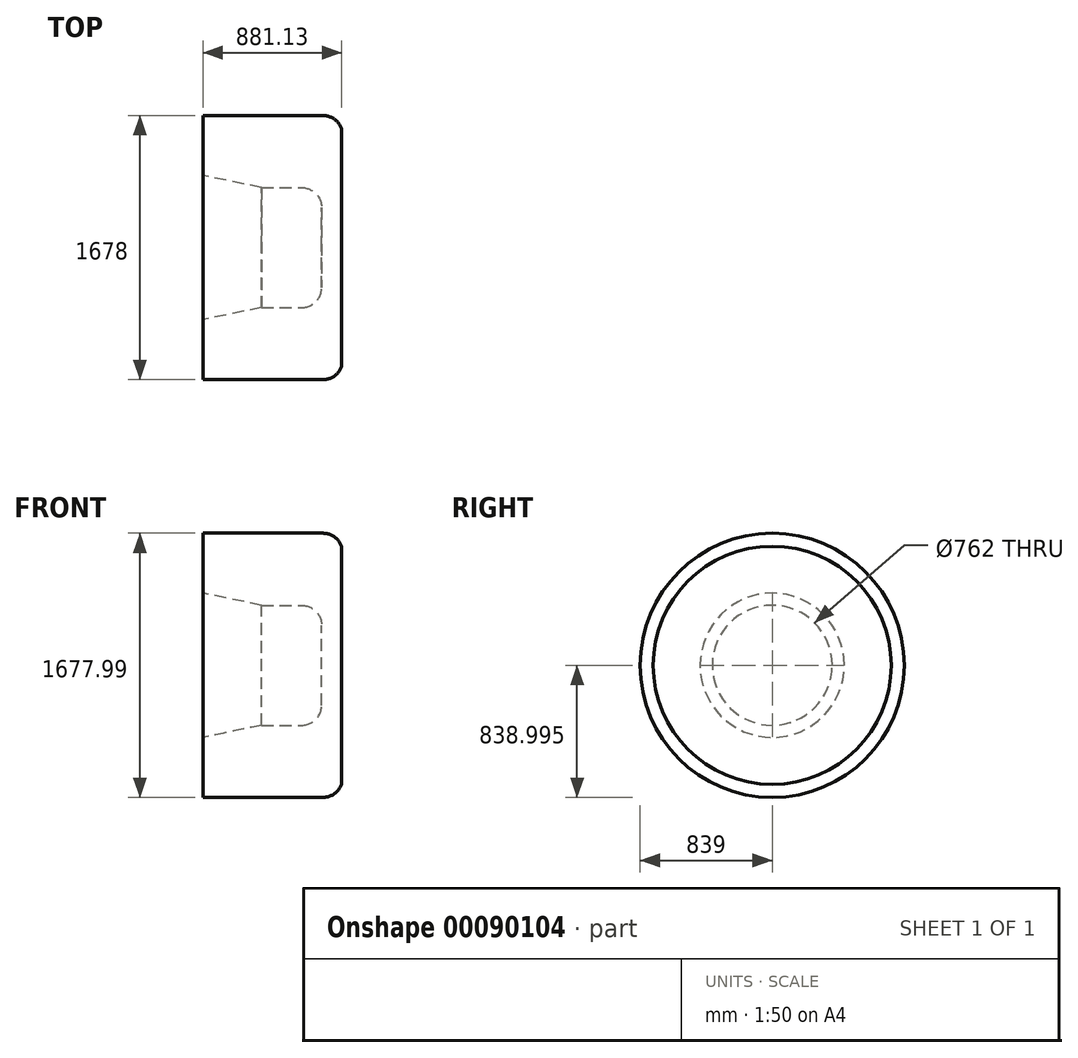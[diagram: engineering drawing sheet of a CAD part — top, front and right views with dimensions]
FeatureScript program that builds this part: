
annotation { "Feature Type Name" : "Feature", "Feature Type Description" : "" }
export const myFeature = defineFeature(function(context is Context, id is Id, definition is map)
    precondition{}
    {
        {
            var Q0;
            Q0=qCreatedBy(makeId("Front.planeOp"),FACE);
            var sketch = newSketch(context, id + "F0", { "sketchPlane" : qUnion([Q0])});
            skLineSegment(sketch, "E0", {"start": v(-424.15, -48.11) * mm, "end": v(-424.15, -429.11) * mm});
            skLineSegment(sketch, "E1", {"start": v(-424.15, -429.11) * mm, "end": v(337.85, -429.11) * mm});
            skArc(sketch, "E2", {"start": v(337.85, -429.11) * mm, "mid": v(410.45, -406.31) * mm, "end": v(456.98, -346.1) * mm});
            skLineSegment(sketch, "E3", {"start": v(456.98, -346.1) * mm, "end": v(456.98, 409.88) * mm});
            skLineSegment(sketch, "E4", {"start": v(456.98, 409.88) * mm, "end": v(329.98, 409.88) * mm});
            skLineSegment(sketch, "E5", {"start": v(329.98, 409.88) * mm, "end": v(329.98, 155.88) * mm});
            skArc(sketch, "E6", {"start": v(202.98, 28.88) * mm, "mid": v(292.79, 66.08) * mm, "end": v(329.98, 155.88) * mm});
            skLineSegment(sketch, "E7", {"start": v(202.98, 28.88) * mm, "end": v(-51.02, 28.88) * mm});
            skLineSegment(sketch, "E8", {"start": v(-51.02, 28.88) * mm, "end": v(-424.15, -48.11) * mm});
            skSolve(sketch);
        }
        {
            var Q0;
            Q0=makeQuery(id+"F0.imprint","IMPRINT",FACE,{"disambiguationData":[TD([[makeQuery(id+"F0.imprint","IMPRINT",EDGE,{"derivedFrom":sQuery(id+"F0.wireOp",EDGE,"E0")}),1.0]])]});
            var Q1;
            Q1=sQuery(id+"F0.wireOp",EDGE,"E4");
            revolve(context, id + "F1", {"entities" : qUnion([Q0]), "axis" : qUnion([Q1]), "revolveType" : RevolveType.FULL});
        }
    });
